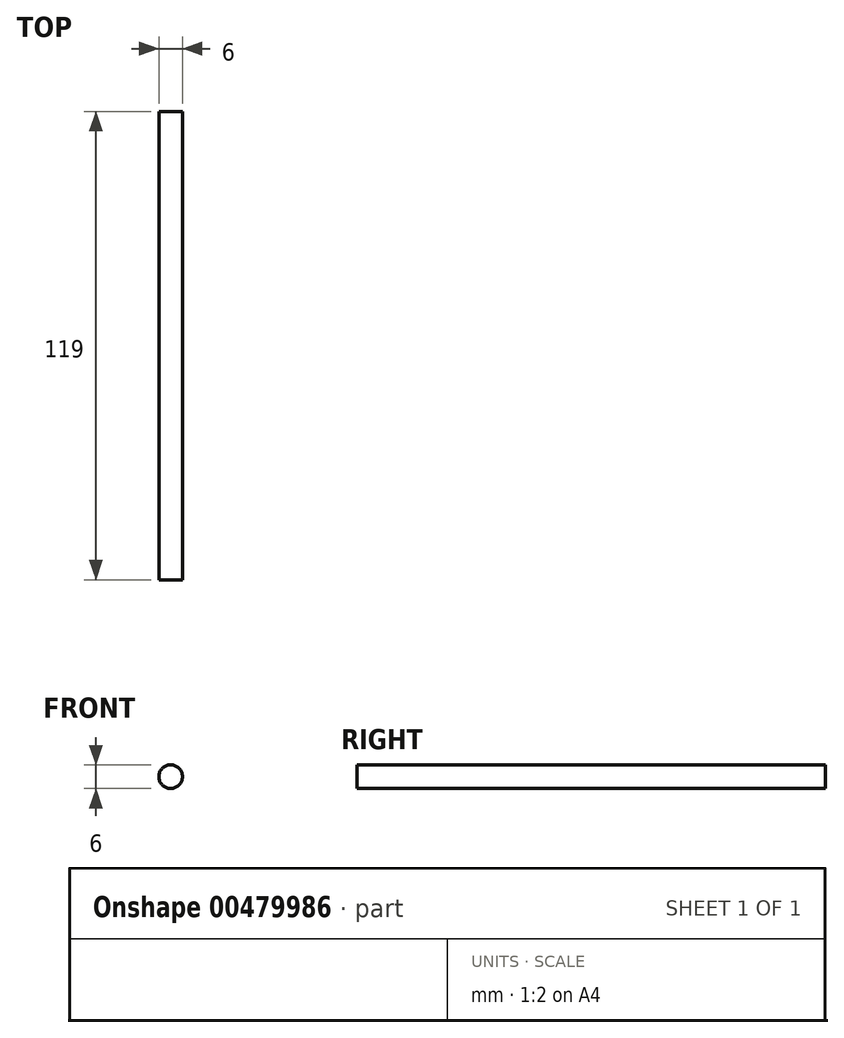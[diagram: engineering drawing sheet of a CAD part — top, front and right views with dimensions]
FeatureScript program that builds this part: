
annotation { "Feature Type Name" : "Feature", "Feature Type Description" : "" }
export const myFeature = defineFeature(function(context is Context, id is Id, definition is map)
    precondition{}
    {
        {
            var Q0;
            Q0=qCreatedBy(makeId("Front.planeOp"),FACE);
            var sketch = newSketch(context, id + "F0", { "sketchPlane" : qUnion([Q0])});
            skCircle(sketch, "E0", {"center": v(0, 0) * mm, "radius": 3 * mm});
            skSolve(sketch);
        }
        {
            var Q0;
            Q0=makeQuery(id+"F0.imprint","IMPRINT",FACE,{"disambiguationData":[TD([[makeQuery(id+"F0.imprint","IMPRINT",EDGE,{"derivedFrom":sQuery(id+"F0.wireOp",EDGE,"E0")}),1.0]])]});
            extrude(context, id + "F1", {"entities" : qUnion([Q0]), "depth" : 119 * mm});
        }
    });
